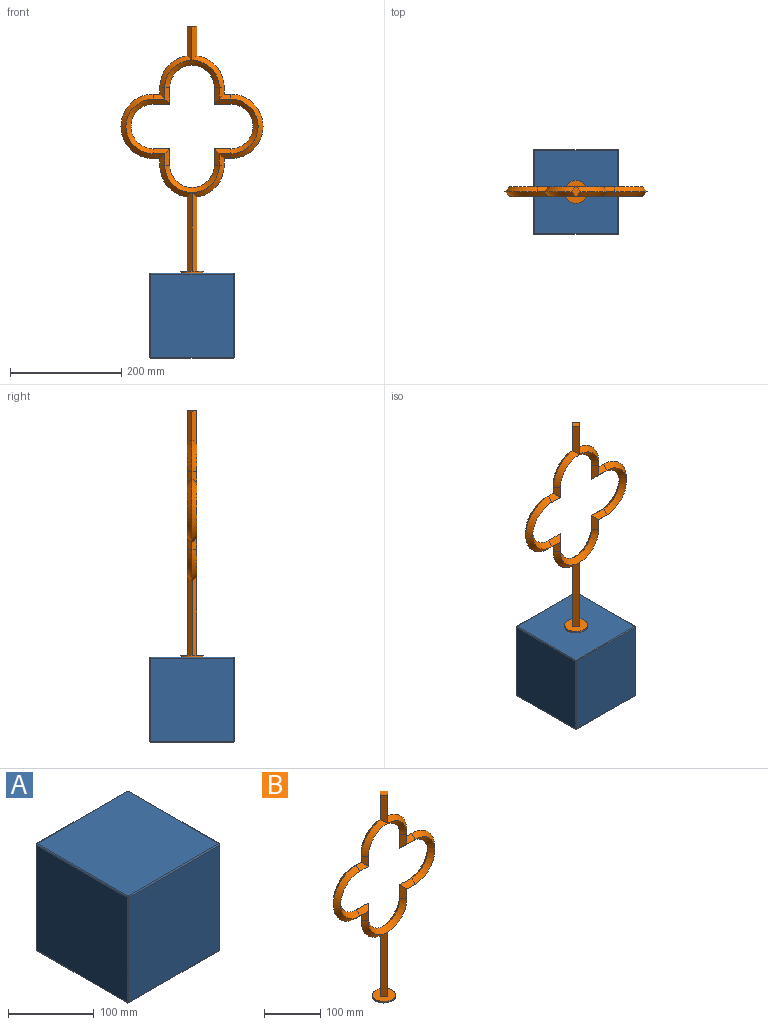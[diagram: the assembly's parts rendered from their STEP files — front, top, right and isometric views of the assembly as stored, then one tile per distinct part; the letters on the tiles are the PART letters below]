
ASSEMBLY  parts=2 mates=1
PART A: 26 faces, bbox 152.4x152.4x152.4 mm
  f0: plane 149.23x149.23mm, normal (-1,0,0), area 22268.1mm2, adj f14,f19,f22,f25
  f1: plane 149.23x149.23mm, normal (0,0,-1), area 22268.1mm2, adj f11,f20,f21,f25
  f2: plane 149.23x149.23mm, normal (1,0,0), area 22268.1mm2, adj f6,f10,f11,f12
  f3: plane 149.23x149.23mm, normal (0,0,1), area 22268.1mm2, adj f6,f9,f13,f14
  f4: plane 149.23x149.23mm, normal (0,-1,0), area 22268.1mm2, adj f9,f10,f19,f20
  f5: plane 149.23x149.23mm, normal (0,1,0), area 22268.1mm2, adj f12,f13,f21,f22
  f6: cylinder r=1.59mm len=149.23mm, axis (0,-1,0), area 372.1mm2, adj f2,f3,f7,f8
  f7: sphere r=1.59mm, area 4mm2, adj f6,f9,f10
  f8: sphere r=1.59mm, area 4mm2, adj f6,f12,f13
  f9: cylinder r=1.59mm len=149.23mm, axis (1,0,0), area 372.1mm2, adj f3,f4,f7,f15
  f10: cylinder r=1.59mm len=149.23mm, axis (0,0,-1), area 372.1mm2, adj f2,f4,f7,f16
  f11: cylinder r=1.59mm len=149.23mm, axis (0,1,0), area 372.1mm2, adj f1,f2,f16,f17
  f12: cylinder r=1.59mm len=149.23mm, axis (0,0,1), area 372.1mm2, adj f2,f5,f8,f17
  f13: cylinder r=1.59mm len=149.23mm, axis (-1,0,0), area 372.1mm2, adj f3,f5,f8,f18
  f14: cylinder r=1.59mm len=149.23mm, axis (0,1,0), area 372.1mm2, adj f0,f3,f15,f18
  f15: sphere r=1.59mm, area 4mm2, adj f9,f14,f19
  f16: sphere r=1.59mm, area 4mm2, adj f10,f11,f20
  f17: sphere r=1.59mm, area 4mm2, adj f11,f12,f21
  f18: sphere r=1.59mm, area 4mm2, adj f13,f14,f22
  f19: cylinder r=1.59mm len=149.23mm, axis (0,0,1), area 372.1mm2, adj f0,f4,f15,f23
  f20: cylinder r=1.59mm len=149.23mm, axis (-1,0,0), area 372.1mm2, adj f1,f4,f16,f23
  f21: cylinder r=1.59mm len=149.23mm, axis (1,0,0), area 372.1mm2, adj f1,f5,f17,f24
  f22: cylinder r=1.59mm len=149.23mm, axis (0,0,-1), area 372.1mm2, adj f0,f5,f18,f24
  f23: sphere r=1.59mm, area 4mm2, adj f19,f20,f25
  f24: sphere r=1.59mm, area 4mm2, adj f21,f22,f25
  f25: cylinder r=1.59mm len=149.23mm, axis (0,-1,0), area 372.1mm2, adj f0,f1,f23,f24
PART B: 64 faces, bbox 255.6x41.3x444.5 mm
  f0: plane 61.77x8.98mm, normal (0.71,0.71,0), area 730.6mm2, adj f1,f2,f3,f8
  f1: plane 17.96x17.96mm, normal (0,0,1), area 161.3mm2, adj f0,f2,f3,f4
  f2: plane 61.77x8.98mm, normal (0.71,-0.71,0), area 730.6mm2, adj f0,f1,f4,f6
  f3: plane 61.77x8.98mm, normal (-0.71,0.71,0), area 730.6mm2, adj f0,f1,f4,f7
  f4: plane 61.77x8.98mm, normal (-0.71,-0.71,0), area 730.6mm2, adj f1,f2,f3,f5
  f5: cone r=48.95mm half-angle=45deg, axis (0,1,0), area 1008.9mm2, adj f4,f7,f59,f60
  f6: cone r=48.95mm half-angle=45deg, axis (0,1,0), area 1008.9mm2, adj f2,f8,f54,f59
  f7: cone r=57.93mm half-angle=45deg, axis (0,-1,0), area 1008.9mm2, adj f3,f5,f58,f61
  f8: cone r=57.93mm half-angle=45deg, axis (0,-1,0), area 1008.9mm2, adj f0,f6,f55,f58
  f9: plane 0.46x0.23mm, normal (0,0,1), area 0.1mm2, adj f13,f16,f22
  f10: plane 41.28x41.28mm, normal (0,0,1), area 1176.7mm2, adj f11,f13,f14,f15,f16
  f11: cylinder r=20.64mm len=41.28mm, axis (0,0,-1), area 411.7mm2, adj f10,f12
  f12: plane 41.28x41.28mm, normal (0,0,-1), area 1338mm2, adj f11
  f13: plane 141.73x8.98mm, normal (0.71,-0.71,0), area 1748.9mm2, adj f9,f10,f14,f16,f22
  f14: plane 141.73x8.98mm, normal (0.71,0.71,0), area 1748.9mm2, adj f10,f13,f15,f17,f23
  f15: plane 141.73x8.98mm, normal (-0.71,0.71,0), area 1748.9mm2, adj f10,f14,f16,f17,f23
  f16: plane 141.73x8.98mm, normal (-0.71,-0.71,0), area 1748.9mm2, adj f9,f10,f13,f15,f22
  f17: plane 0.46x0.23mm, normal (0,0,1), area 0.1mm2, adj f14,f15,f23
  f18: plane 20.9x8.98mm, normal (-0.71,-0.71,0), area 208.5mm2, adj f19,f21,f22,f50
  f19: plane 20.9x8.98mm, normal (-0.71,0.71,0), area 208.5mm2, adj f18,f20,f23,f51
  f20: plane 29.88x8.98mm, normal (0.71,0.71,0), area 322.5mm2, adj f19,f21,f24,f52
  f21: plane 29.88x8.98mm, normal (0.71,-0.71,0), area 322.5mm2, adj f18,f20,f25,f53
  f22: cone r=48.95mm half-angle=45deg, axis (0,1,0), area 2017.8mm2, adj f9,f13,f16,f18,f23,f25,f26
  f23: cone r=57.93mm half-angle=45deg, axis (0,-1,0), area 2017.8mm2, adj f14,f15,f17,f19,f22,f24,f27
  f24: cone r=48.95mm half-angle=45deg, axis (0,1,0), area 1773.7mm2, adj f20,f23,f25,f28
  f25: cone r=39.97mm half-angle=45deg, axis (0,-1,0), area 1773.7mm2, adj f21,f22,f24,f29
  f26: plane 20.9x8.98mm, normal (0.71,-0.71,0), area 208.5mm2, adj f22,f27,f29,f30
  f27: plane 20.9x8.98mm, normal (0.71,0.71,0), area 208.5mm2, adj f23,f26,f28,f31
  f28: plane 29.88x8.98mm, normal (-0.71,0.71,0), area 322.5mm2, adj f24,f27,f29,f32
  f29: plane 29.88x8.98mm, normal (-0.71,-0.71,0), area 322.5mm2, adj f25,f26,f28,f33
  f30: plane 20.9x8.98mm, normal (0,-0.71,-0.71), area 208.5mm2, adj f26,f31,f33,f34
  f31: plane 20.9x8.98mm, normal (0,0.71,-0.71), area 208.5mm2, adj f27,f30,f32,f35
  f32: plane 29.88x8.98mm, normal (0,0.71,0.71), area 322.5mm2, adj f28,f31,f33,f36
  f33: plane 29.88x8.98mm, normal (0,-0.71,0.71), area 322.5mm2, adj f29,f30,f32,f37
  f34: cone r=48.95mm half-angle=45deg, axis (0,1,0), area 2132mm2, adj f30,f35,f37,f38
  f35: cone r=57.93mm half-angle=45deg, axis (0,-1,0), area 2132mm2, adj f31,f34,f36,f39
  f36: cone r=48.95mm half-angle=45deg, axis (0,1,0), area 1773.7mm2, adj f32,f35,f37,f40
  f37: cone r=39.97mm half-angle=45deg, axis (0,-1,0), area 1773.7mm2, adj f33,f34,f36,f41
  f38: plane 20.9x8.98mm, normal (0,-0.71,0.71), area 208.5mm2, adj f34,f39,f41,f54
  f39: plane 20.9x8.98mm, normal (0,0.71,0.71), area 208.5mm2, adj f35,f38,f40,f55
  f40: plane 29.88x8.98mm, normal (0,0.71,-0.71), area 322.5mm2, adj f36,f39,f41,f56
  f41: plane 29.88x8.98mm, normal (0,-0.71,-0.71), area 322.5mm2, adj f37,f38,f40,f57
  f42: plane 20.9x8.98mm, normal (0,-0.71,0.71), area 208.5mm2, adj f43,f45,f46,f60
  f43: plane 20.9x8.98mm, normal (0,0.71,0.71), area 208.5mm2, adj f42,f44,f47,f61
  f44: plane 29.88x8.98mm, normal (0,0.71,-0.71), area 322.5mm2, adj f43,f45,f48,f62
  f45: plane 29.88x8.98mm, normal (0,-0.71,-0.71), area 322.5mm2, adj f42,f44,f49,f63
  f46: cone r=48.95mm half-angle=45deg, axis (0,1,0), area 2132mm2, adj f42,f47,f49,f50
  f47: cone r=57.93mm half-angle=45deg, axis (0,-1,0), area 2132mm2, adj f43,f46,f48,f51
  f48: cone r=48.95mm half-angle=45deg, axis (0,1,0), area 1773.7mm2, adj f44,f47,f49,f52
  f49: cone r=39.97mm half-angle=45deg, axis (0,-1,0), area 1773.7mm2, adj f45,f46,f48,f53
  f50: plane 20.9x8.98mm, normal (0,-0.71,-0.71), area 208.5mm2, adj f18,f46,f51,f53
  f51: plane 20.9x8.98mm, normal (0,0.71,-0.71), area 208.5mm2, adj f19,f47,f50,f52
  f52: plane 29.88x8.98mm, normal (0,0.71,0.71), area 322.5mm2, adj f20,f48,f51,f53
  f53: plane 29.88x8.98mm, normal (0,-0.71,0.71), area 322.5mm2, adj f21,f49,f50,f52
  f54: plane 20.9x8.98mm, normal (0.71,-0.71,0), area 208.5mm2, adj f6,f38,f55,f57
  f55: plane 20.9x8.98mm, normal (0.71,0.71,0), area 208.5mm2, adj f8,f39,f54,f56
  f56: plane 29.88x8.98mm, normal (-0.71,0.71,0), area 322.5mm2, adj f40,f55,f57,f58
  f57: plane 29.88x8.98mm, normal (-0.71,-0.71,0), area 322.5mm2, adj f41,f54,f56,f59
  f58: cone r=48.95mm half-angle=45deg, axis (0,1,0), area 1773.7mm2, adj f7,f8,f56,f59,f62
  f59: cone r=39.97mm half-angle=45deg, axis (0,-1,0), area 1773.7mm2, adj f5,f6,f57,f58,f63
  f60: plane 20.9x8.98mm, normal (-0.71,-0.71,0), area 208.5mm2, adj f5,f42,f61,f63
  f61: plane 20.9x8.98mm, normal (-0.71,0.71,0), area 208.5mm2, adj f7,f43,f60,f62
  f62: plane 29.88x8.98mm, normal (0.71,0.71,0), area 322.5mm2, adj f44,f58,f61,f63
  f63: plane 29.88x8.98mm, normal (0.71,-0.71,0), area 322.5mm2, adj f45,f59,f60,f62
PLACE A t=(-5.46,-2.05,127.29)mm
PLACE B t=(-5.46,-2.05,279.69)mm
MATE fastened A.f3 <-> B.f11  axis (0,0,1) through (-5.46,-2.05,279.69)mm
